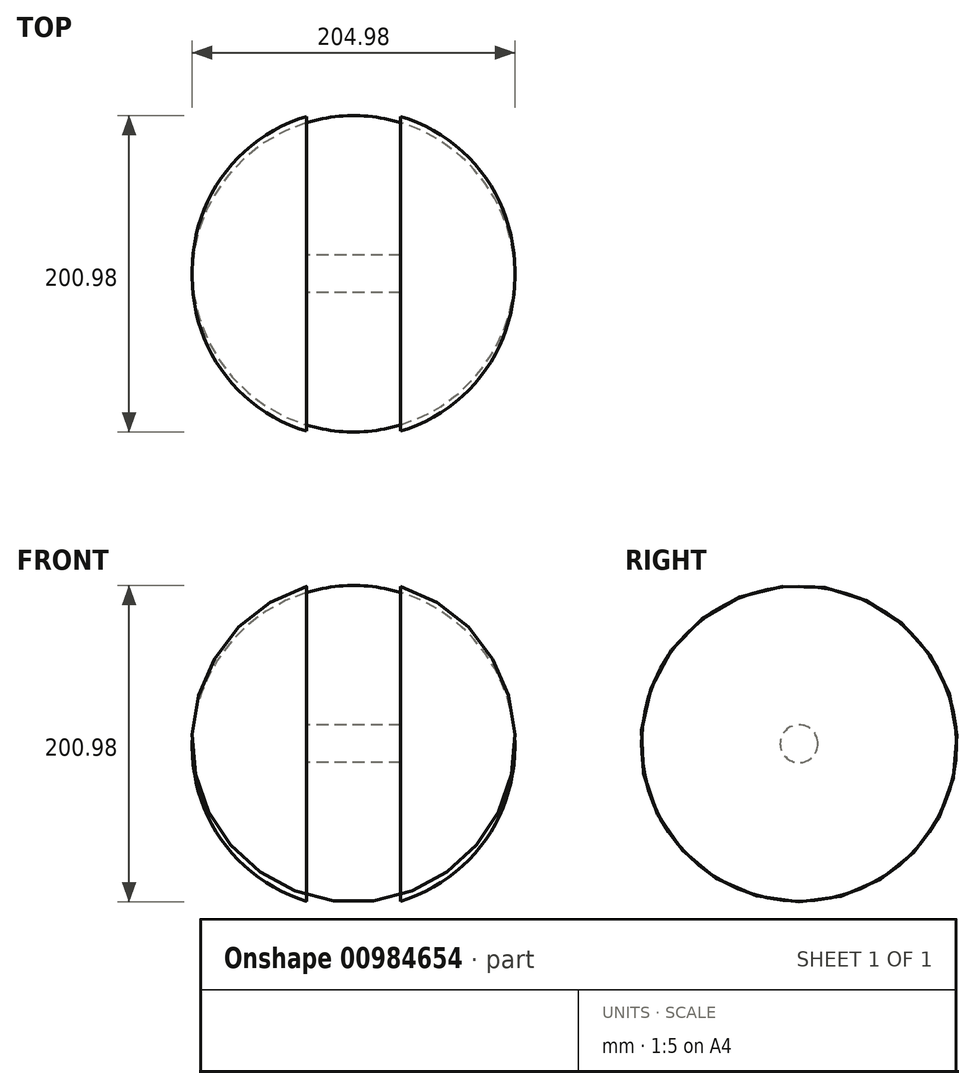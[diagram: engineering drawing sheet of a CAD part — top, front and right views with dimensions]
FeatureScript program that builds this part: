
annotation { "Feature Type Name" : "Feature", "Feature Type Description" : "" }
export const myFeature = defineFeature(function(context is Context, id is Id, definition is map)
    precondition{}
    {
        {
            var Q0;
            Q0=qCreatedBy(makeId("Front.planeOp"),FACE);
            var sketch = newSketch(context, id + "F0", { "sketchPlane" : qUnion([Q0])});
            skLineSegment(sketch, "E0", {"start": v(0, 0) * mm, "end": v(0, 12) * mm, "construction": true});
            skLineSegment(sketch, "E1", {"start": v(0, 12) * mm, "end": v(60, 12) * mm});
            skLineSegment(sketch, "E2", {"start": v(60, 12) * mm, "end": v(60, 100) * mm});
            skLineSegment(sketch, "E3", {"start": v(0, 12) * mm, "end": v(0, 100) * mm});
            skArc(sketch, "E4", {"start": v(60, 100) * mm, "mid": v(30, 104.49) * mm, "end": v(0, 100) * mm});
            skPoint(sketch, "E4.first.point", {"position": v(30, 0) * mm});
            skPoint(sketch, "E4.first.point.positionSnap0", {"position": v(30, 12) * mm});
            skSolve(sketch);
        }
        {
            var Q0;
            Q0=qCreatedBy(makeId("Front.planeOp"),FACE);
            var sketch = newSketch(context, id + "F1", { "sketchPlane" : qUnion([Q0])});
            skLineSegment(sketch, "E5", {"start": v(-31.73, 0) * mm, "end": v(100.92, 0) * mm, "construction": true});
            skSolve(sketch);
        }
        {
            var Q0;
            Q0=makeQuery(id+"F0.imprint","IMPRINT",FACE,{"disambiguationData":[TD([[makeQuery(id+"F0.imprint","IMPRINT",EDGE,{"derivedFrom":sQuery(id+"F0.wireOp",EDGE,"E1")}),1.0]])]});
            var Q1;
            Q1=sQuery(id+"F1.wireOp",EDGE,"E5");
            revolve(context, id + "F2", {"surfaceOperationType" : NewSurfaceOperationType.NEW, "entities" : qUnion([Q0]), "axis" : qUnion([Q1]), "revolveType" : RevolveType.FULL});
        }
    });
